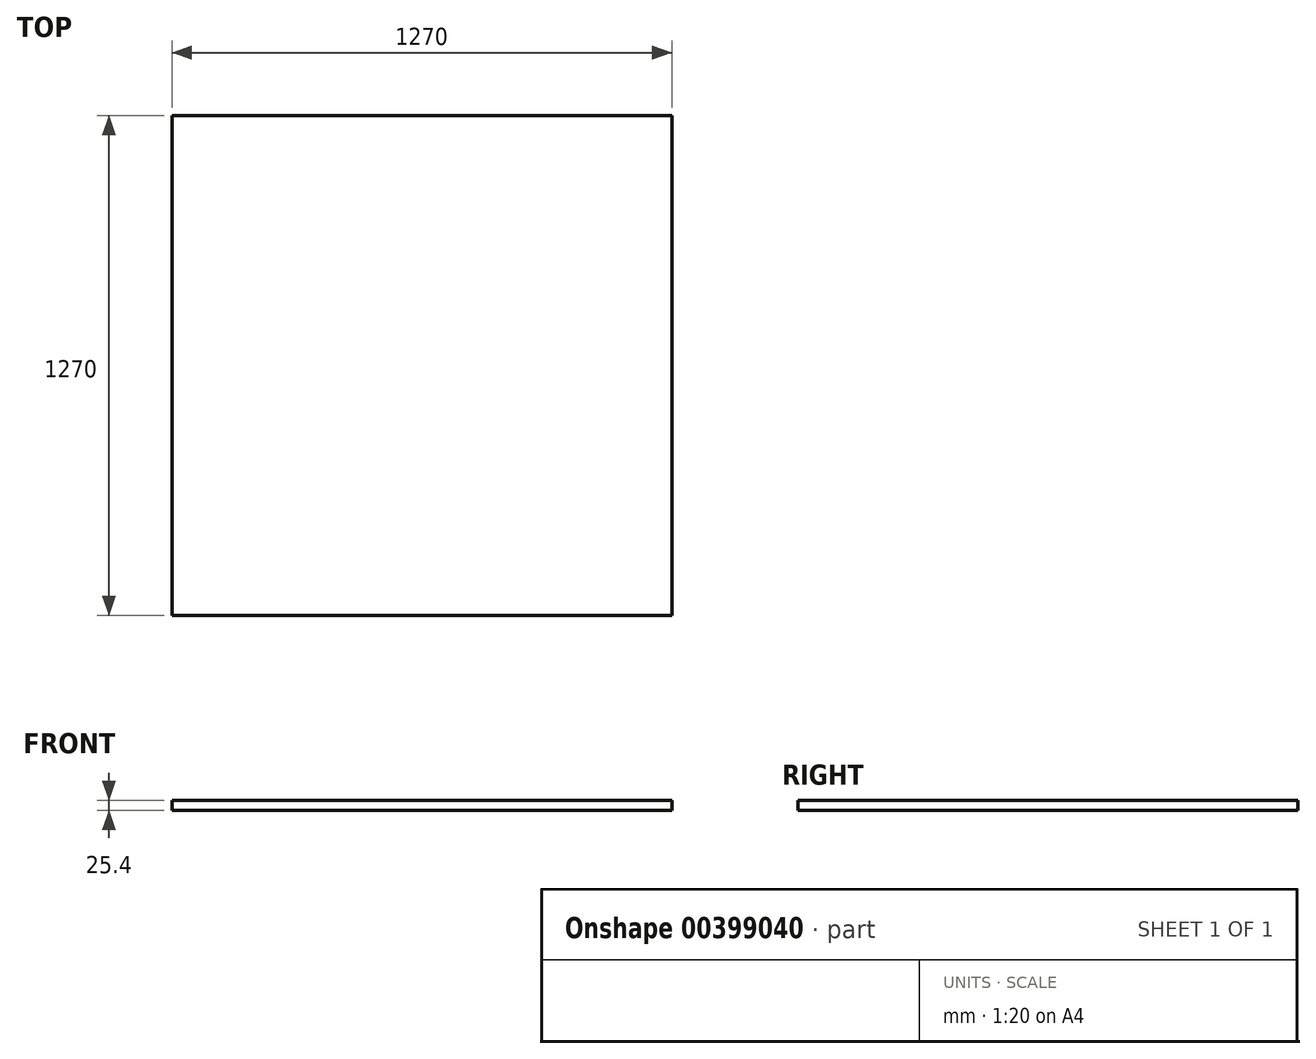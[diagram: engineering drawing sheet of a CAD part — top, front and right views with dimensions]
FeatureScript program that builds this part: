
annotation { "Feature Type Name" : "Feature", "Feature Type Description" : "" }
export const myFeature = defineFeature(function(context is Context, id is Id, definition is map)
    precondition{}
    {
        {
            var Q0;
            Q0=qCreatedBy(makeId("Top.planeOp"),FACE);
            var sketch = newSketch(context, id + "F0", { "sketchPlane" : qUnion([Q0])});
            skLineSegment(sketch, "E0.bottom", {"start": v(635, 635) * mm, "end": v(-635, 635) * mm});
            skLineSegment(sketch, "E0.top", {"start": v(635, -635) * mm, "end": v(-635, -635) * mm});
            skLineSegment(sketch, "E0.left", {"start": v(635, 635) * mm, "end": v(635, -635) * mm});
            skLineSegment(sketch, "E0.right", {"start": v(-635, 635) * mm, "end": v(-635, -635) * mm});
            skPoint(sketch, "E0.middle", {"position": v(0, 0) * mm});
            skSolve(sketch);
        }
        {
            var Q0;
            Q0 = qSketchRegion(id + "F0", true);
            extrude(context, id + "F1", {"entities" : qUnion([Q0]), "depth" : 25.4 * mm});
        }
    });
